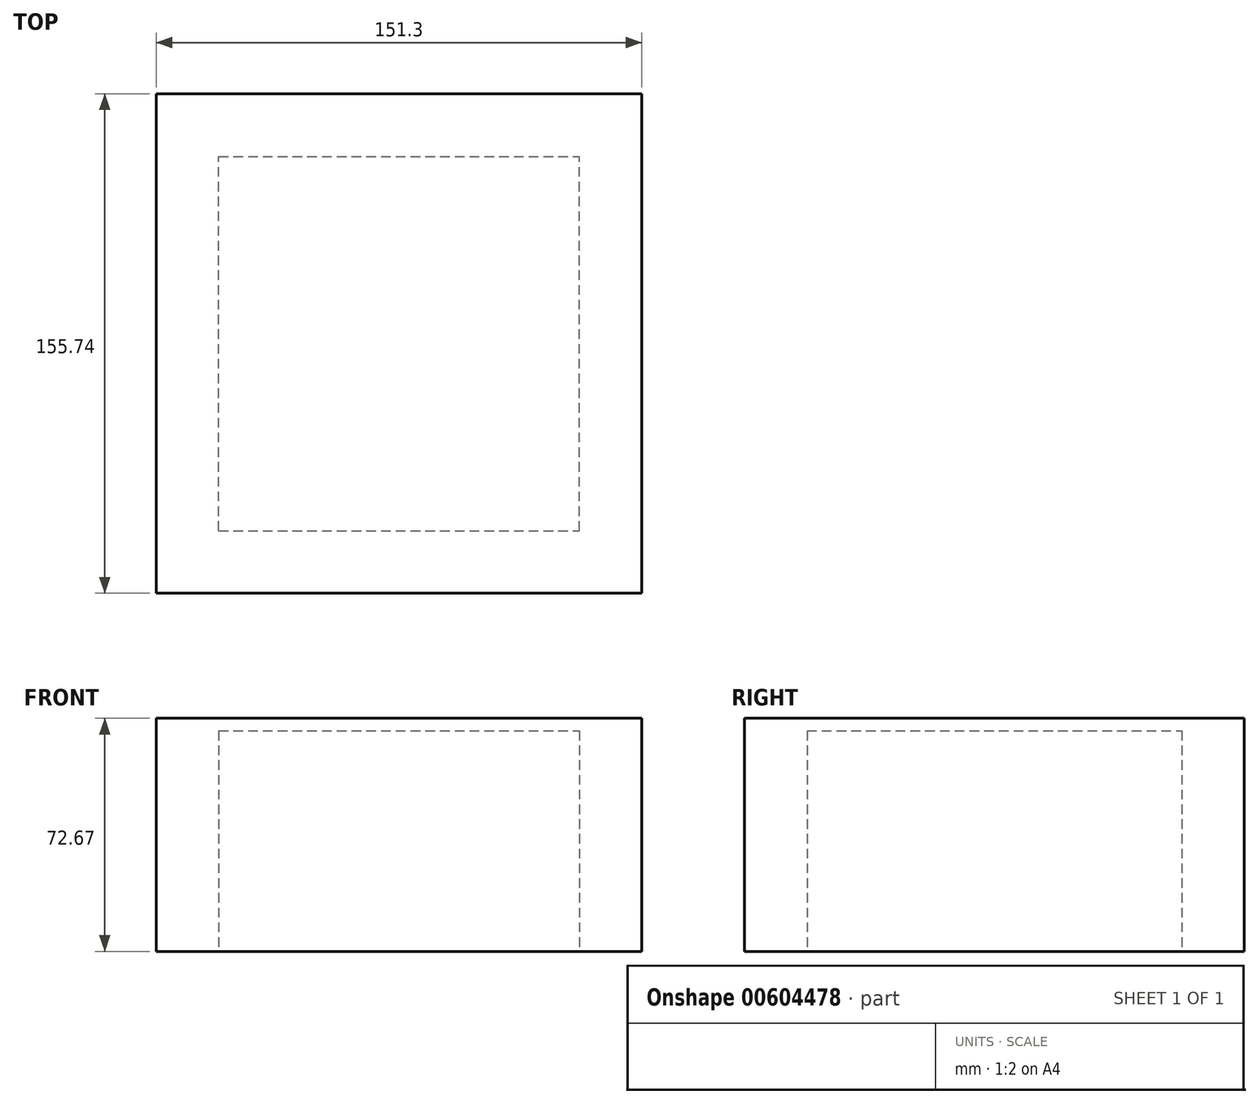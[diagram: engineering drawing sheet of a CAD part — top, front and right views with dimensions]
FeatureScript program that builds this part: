
annotation { "Feature Type Name" : "Feature", "Feature Type Description" : "" }
export const myFeature = defineFeature(function(context is Context, id is Id, definition is map)
    precondition{}
    {
        {
            var Q0;
            Q0=qCreatedBy(makeId("Top.planeOp"),FACE);
            var sketch = newSketch(context, id + "F0", { "sketchPlane" : qUnion([Q0])});
            skLineSegment(sketch, "E0.bottom", {"start": v(75.65, -77.87) * mm, "end": v(-75.65, -77.87) * mm});
            skLineSegment(sketch, "E0.top", {"start": v(75.65, 77.87) * mm, "end": v(-75.65, 77.87) * mm});
            skLineSegment(sketch, "E0.left", {"start": v(75.65, -77.87) * mm, "end": v(75.65, 77.87) * mm});
            skLineSegment(sketch, "E0.right", {"start": v(-75.65, -77.87) * mm, "end": v(-75.65, 77.87) * mm});
            skPoint(sketch, "E0.middle", {"position": v(0, 0) * mm});
            skSolve(sketch);
        }
        {
            var Q0;
            Q0=makeQuery(id+"F0.imprint","IMPRINT",FACE,{"disambiguationData":[TD([[makeQuery(id+"F0.imprint","IMPRINT",EDGE,{"derivedFrom":sQuery(id+"F0.wireOp",EDGE,"E0.bottom")}),-1.0]])]});
            extrude(context, id + "F1", {"entities" : qUnion([Q0]), "depth" : 72.67 * mm, "offsetDistance" : 25.4 * mm});
        }
        {
            var Q0;
            Q0=makeQuery(id+"F1.opExtrude","CAP_FACE",FACE,{"disambiguationData":[OSD([sQuery(id+"F0.wireOp",EDGE,"E0.bottom"),sQuery(id+"F0.wireOp",EDGE,"E0.top"),sQuery(id+"F0.wireOp",EDGE,"E0.left"),sQuery(id+"F0.wireOp",EDGE,"E0.right")])],"isStart":true});
            var sketch = newSketch(context, id + "F2", { "sketchPlane" : qUnion([Q0])});
            skLineSegment(sketch, "E1.bottom", {"start": v(-56.16, 58.37) * mm, "end": v(56.16, 58.37) * mm});
            skLineSegment(sketch, "E1.top", {"start": v(-56.16, -58.37) * mm, "end": v(56.16, -58.37) * mm});
            skLineSegment(sketch, "E1.left", {"start": v(-56.16, 58.37) * mm, "end": v(-56.16, -58.37) * mm});
            skLineSegment(sketch, "E1.right", {"start": v(56.16, 58.37) * mm, "end": v(56.16, -58.37) * mm});
            skPoint(sketch, "E1.middle", {"position": v(0, 0) * mm});
            skSolve(sketch);
        }
        {
            var Q0;
            Q0=makeQuery(id+"F2.imprint","IMPRINT",FACE,{"disambiguationData":[TD([[makeQuery(id+"F2.imprint","IMPRINT",EDGE,{"derivedFrom":sQuery(id+"F2.wireOp",EDGE,"E1.bottom")}),-1.0]])]});
            extrude(context, id + "F3", {"entities" : qUnion([Q0]), "operationType" : NewBodyOperationType.REMOVE, "oppositeDirection" : true, "depth" : 68.8 * mm, "offsetDistance" : 25.4 * mm});
        }
    });
